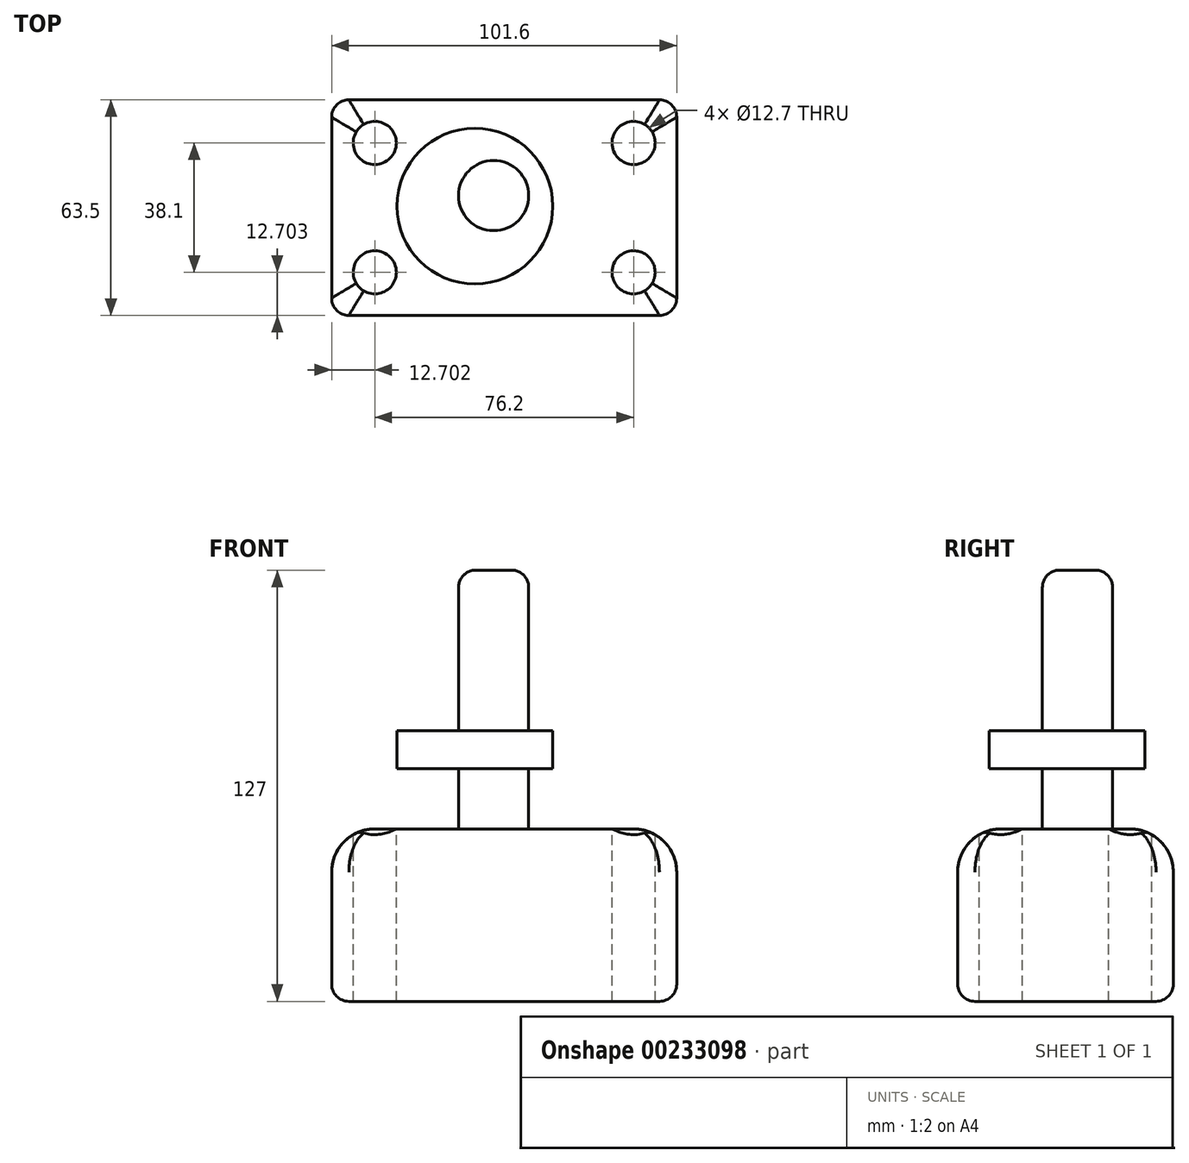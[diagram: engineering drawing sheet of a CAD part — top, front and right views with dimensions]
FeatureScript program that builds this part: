
annotation { "Feature Type Name" : "Feature", "Feature Type Description" : "" }
export const myFeature = defineFeature(function(context is Context, id is Id, definition is map)
    precondition{}
    {
        {
            var Q0;
            Q0=qCreatedBy(makeId("Top.planeOp"),FACE);
            var sketch = newSketch(context, id + "F0", { "sketchPlane" : qUnion([Q0])});
            skLineSegment(sketch, "E0.bottom", {"start": v(-47.69, 31.32) * mm, "end": v(53.91, 31.32) * mm});
            skLineSegment(sketch, "E0.top", {"start": v(-47.69, -32.18) * mm, "end": v(53.91, -32.18) * mm});
            skLineSegment(sketch, "E0.left", {"start": v(-47.69, 31.32) * mm, "end": v(-47.69, -32.18) * mm});
            skLineSegment(sketch, "E0.right", {"start": v(53.91, 31.32) * mm, "end": v(53.91, -32.18) * mm});
            skSolve(sketch);
        }
        {
            var Q0;
            Q0 = qSketchRegion(id + "F0", true);
            extrude(context, id + "F1", {"entities" : qUnion([Q0]), "depth" : 50.8 * mm});
        }
        {
            var Q0;
            Q0=makeQuery(id+"F1.opExtrude","CAP_FACE",FACE,{"disambiguationData":[OSD([sQuery(id+"F0.wireOp",EDGE,"E0.bottom"),sQuery(id+"F0.wireOp",EDGE,"E0.top"),sQuery(id+"F0.wireOp",EDGE,"E0.left"),sQuery(id+"F0.wireOp",EDGE,"E0.right")])],"isStart":false});
            var sketch = newSketch(context, id + "F2", { "sketchPlane" : qUnion([Q0])});
            skCircle(sketch, "E1", {"center": v(-34.99, 18.62) * mm, "radius": 6.35 * mm});
            skCircle(sketch, "E2", {"center": v(41.21, 18.62) * mm, "radius": 6.35 * mm});
            skCircle(sketch, "E3", {"center": v(-34.99, -19.48) * mm, "radius": 6.35 * mm});
            skCircle(sketch, "E4", {"center": v(41.21, -19.48) * mm, "radius": 6.35 * mm});
            skSolve(sketch);
        }
        {
            var Q0;
            Q0=makeQuery(id+"F2.imprint","IMPRINT",FACE,{"disambiguationData":[TD([[makeQuery(id+"F2.imprint","IMPRINT",EDGE,{"derivedFrom":sQuery(id+"F2.wireOp",EDGE,"E3")}),1.0]])]});
            var Q1;
            Q1=makeQuery(id+"F2.imprint","IMPRINT",FACE,{"disambiguationData":[TD([[makeQuery(id+"F2.imprint","IMPRINT",EDGE,{"derivedFrom":sQuery(id+"F2.wireOp",EDGE,"E1")}),1.0]])]});
            var Q2;
            Q2=makeQuery(id+"F2.imprint","IMPRINT",FACE,{"disambiguationData":[TD([[makeQuery(id+"F2.imprint","IMPRINT",EDGE,{"derivedFrom":sQuery(id+"F2.wireOp",EDGE,"E2")}),1.0]])]});
            var Q3;
            Q3=makeQuery(id+"F2.imprint","IMPRINT",FACE,{"disambiguationData":[TD([[makeQuery(id+"F2.imprint","IMPRINT",EDGE,{"derivedFrom":sQuery(id+"F2.wireOp",EDGE,"E4")}),1.0]])]});
            var Q4;
            Q4=sQuery(id+"F2.wireOp",EDGE,"E1");
            var Q5;
            Q5=sQuery(id+"F2.wireOp",EDGE,"E2");
            var Q6;
            Q6=sQuery(id+"F2.wireOp",EDGE,"E3");
            var Q7;
            Q7=sQuery(id+"F2.wireOp",EDGE,"E4");
            extrude(context, id + "F3", {"entities" : qUnion([Q0, Q1, Q2, Q3]), "operationType" : NewBodyOperationType.REMOVE, "surfaceEntities" : qUnion([Q4, Q5, Q6, Q7]), "endBound" : BoundingType.THROUGH_ALL, "oppositeDirection" : true, "depth" : 50.8 * mm});
        }
        {
            var Q0;
            Q0=makeQuery(id+"F1.opExtrude","CAP_FACE",FACE,{"disambiguationData":[OSD([sQuery(id+"F0.wireOp",EDGE,"E0.bottom"),sQuery(id+"F0.wireOp",EDGE,"E0.top"),sQuery(id+"F0.wireOp",EDGE,"E0.left"),sQuery(id+"F0.wireOp",EDGE,"E0.right")])],"isStart":false});
            var sketch = newSketch(context, id + "F4", { "sketchPlane" : qUnion([Q0])});
            skCircle(sketch, "E5", {"center": v(0, 3.12) * mm, "radius": 10.33 * mm});
            skSolve(sketch);
        }
        {
            var Q0;
            Q0=makeQuery(id+"F4.imprint","IMPRINT",FACE,{"disambiguationData":[TD([[makeQuery(id+"F4.imprint","IMPRINT",EDGE,{"derivedFrom":sQuery(id+"F4.wireOp",EDGE,"E5")}),1.0]])]});
            extrude(context, id + "F5", {"entities" : qUnion([Q0]), "operationType" : NewBodyOperationType.ADD, "depth" : 76.2 * mm});
        }
        {
            var Q0;
            Q0=makeQuery(id+"F1.opExtrude","CAP_EDGE",EDGE,{"disambiguationData":[OSD([sQuery(id+"F0.wireOp",EDGE,"E0.top")])],"isStart":false});
            var Q1;
            Q1=makeQuery(id+"F1.opExtrude","CAP_EDGE",EDGE,{"disambiguationData":[OSD([sQuery(id+"F0.wireOp",EDGE,"E0.left")])],"isStart":false});
            var Q2;
            Q2=makeQuery(id+"F1.opExtrude","CAP_EDGE",EDGE,{"disambiguationData":[OSD([sQuery(id+"F0.wireOp",EDGE,"E0.bottom")])],"isStart":false});
            var Q3;
            Q3=makeQuery(id+"F1.opExtrude","CAP_EDGE",EDGE,{"disambiguationData":[OSD([sQuery(id+"F0.wireOp",EDGE,"E0.right")])],"isStart":false});
            fillet(context, id + "F6", {"entities" : qUnion([Q0, Q1, Q2, Q3]), "radius" : 12.7 * mm, "tangentPropagation" : true, "allowEdgeOverflow" : false});
        }
        {
            var Q0;
            Q0=makeQuery(id+"F5.opExtrude","CAP_EDGE",EDGE,{"disambiguationData":[OSD([sQuery(id+"F4.wireOp",EDGE,"E5")])],"isStart":false});
            fillet(context, id + "F7", {"entities" : qUnion([Q0]), "radius" : 5.08 * mm, "tangentPropagation" : true, "allowEdgeOverflow" : false});
        }
        {
            var Q0;
            Q0=makeQuery(id+"F1.opExtrude","SWEPT_EDGE",EDGE,{"disambiguationData":[OSD([sQuery(id+"F0.wireOp",EDGE,"E0.top"),sQuery(id+"F0.wireOp",EDGE,"E0.right")])]});
            var Q1;
            Q1=makeQuery(id+"F1.opExtrude","SWEPT_EDGE",EDGE,{"disambiguationData":[OSD([sQuery(id+"F0.wireOp",EDGE,"E0.top"),sQuery(id+"F0.wireOp",EDGE,"E0.left")])]});
            var Q2;
            Q2=makeQuery(id+"F1.opExtrude","SWEPT_EDGE",EDGE,{"disambiguationData":[OSD([sQuery(id+"F0.wireOp",EDGE,"E0.bottom"),sQuery(id+"F0.wireOp",EDGE,"E0.right")])]});
            var Q3;
            Q3=makeQuery(id+"F1.opExtrude","SWEPT_EDGE",EDGE,{"disambiguationData":[OSD([sQuery(id+"F0.wireOp",EDGE,"E0.bottom"),sQuery(id+"F0.wireOp",EDGE,"E0.left")])]});
            fillet(context, id + "F8", {"entities" : qUnion([Q0, Q1, Q2, Q3]), "radius" : 5.08 * mm, "tangentPropagation" : true, "allowEdgeOverflow" : false});
        }
        {
            var Q0;
            Q0=makeQuery(id+"F1.opExtrude","CAP_EDGE",EDGE,{"disambiguationData":[OSD([sQuery(id+"F0.wireOp",EDGE,"E0.top")])],"isStart":true});
            var Q1;
            Q1=makeQuery(id+"F1.opExtrude","CAP_EDGE",EDGE,{"disambiguationData":[OSD([sQuery(id+"F0.wireOp",EDGE,"E0.right")])],"isStart":true});
            var Q2;
            Q2=makeQuery(id+"F1.opExtrude","CAP_EDGE",EDGE,{"disambiguationData":[OSD([sQuery(id+"F0.wireOp",EDGE,"E0.bottom")])],"isStart":true});
            var Q3;
            Q3=makeQuery(id+"F1.opExtrude","CAP_EDGE",EDGE,{"disambiguationData":[OSD([sQuery(id+"F0.wireOp",EDGE,"E0.left")])],"isStart":true});
            fillet(context, id + "F9", {"entities" : qUnion([Q0, Q1, Q2, Q3]), "radius" : 5.08 * mm, "tangentPropagation" : true, "allowEdgeOverflow" : false});
        }
        {
            var Q0;
            Q0=qCreatedBy(makeId("Front.planeOp"),FACE);
            var sketch = newSketch(context, id + "F10", { "sketchPlane" : qUnion([Q0])});
            skLineSegment(sketch, "E6.bottom", {"start": v(-28.42, 79.76) * mm, "end": v(-5.5, 79.76) * mm});
            skLineSegment(sketch, "E6.top", {"start": v(-28.42, 68.5) * mm, "end": v(-5.5, 68.5) * mm});
            skLineSegment(sketch, "E6.left", {"start": v(-28.42, 79.76) * mm, "end": v(-28.42, 68.5) * mm});
            skLineSegment(sketch, "E6.right", {"start": v(-5.5, 79.76) * mm, "end": v(-5.5, 68.5) * mm});
            skSolve(sketch);
        }
        {
            var Q0;
            Q0=makeQuery(id+"F10.imprint","IMPRINT",FACE,{"disambiguationData":[TD([[makeQuery(id+"F10.imprint","IMPRINT",EDGE,{"derivedFrom":sQuery(id+"F10.wireOp",EDGE,"E6.bottom")}),-1.0]])]});
            var Q1;
            Q1=sQuery(id+"F10.wireOp",EDGE,"E6.right");
            revolve(context, id + "F11", {"operationType" : NewBodyOperationType.ADD, "entities" : qUnion([Q0]), "axis" : qUnion([Q1]), "revolveType" : RevolveType.FULL});
        }
    });
